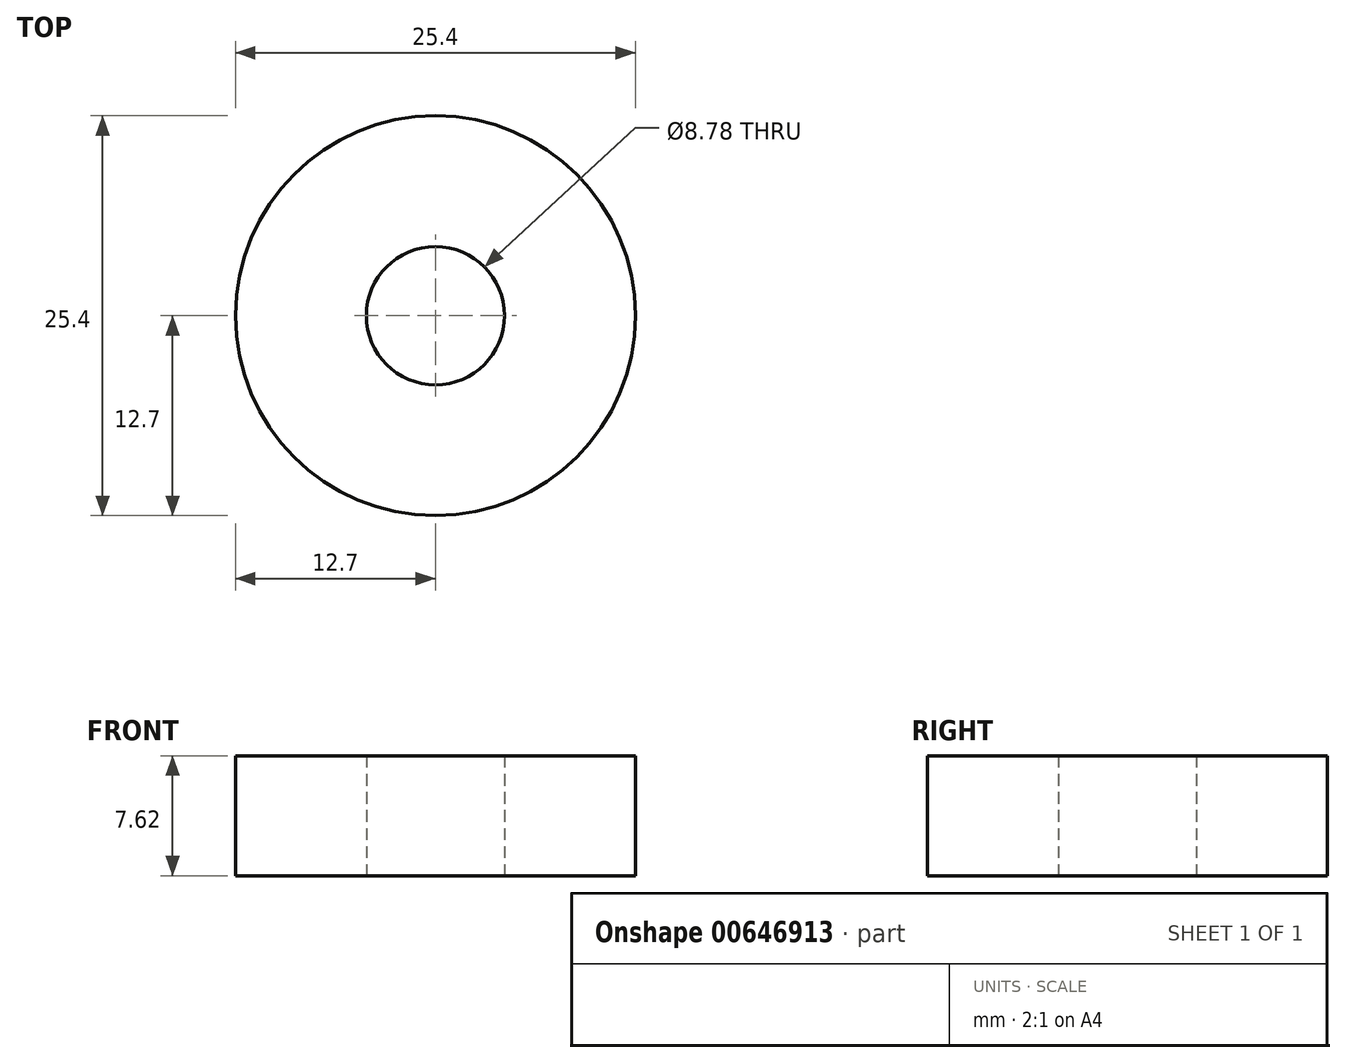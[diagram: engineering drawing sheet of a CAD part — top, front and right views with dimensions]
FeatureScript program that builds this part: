
annotation { "Feature Type Name" : "Feature", "Feature Type Description" : "" }
export const myFeature = defineFeature(function(context is Context, id is Id, definition is map)
    precondition{}
    {
        {
            var Q0;
            Q0=qCreatedBy(makeId("Top.planeOp"),FACE);
            var sketch = newSketch(context, id + "F0", { "sketchPlane" : qUnion([Q0])});
            skCircle(sketch, "E0", {"center": v(0, 0) * mm, "radius": 12.7 * mm});
            skSolve(sketch);
        }
        {
            var Q0;
            Q0 = qSketchRegion(id + "F0", true);
            extrude(context, id + "F1", {"entities" : qUnion([Q0]), "depth" : 7.62 * mm, "offsetDistance" : 25.4 * mm});
        }
        {
            var Q0;
            Q0=makeQuery(id+"F1.opExtrude","CAP_FACE",FACE,{"disambiguationData":[OSD([sQuery(id+"F0.wireOp",EDGE,"E0")])],"isStart":true});
            var sketch = newSketch(context, id + "F2", { "sketchPlane" : qUnion([Q0])});
            skCircle(sketch, "E1", {"center": v(0, 0) * mm, "radius": 4.4 * mm});
            skSolve(sketch);
        }
        {
            var Q0;
            Q0=makeQuery(id+"F2.imprint","IMPRINT",FACE,{"disambiguationData":[TD([[makeQuery(id+"F2.imprint","IMPRINT",EDGE,{"derivedFrom":sQuery(id+"F2.wireOp",EDGE,"E1")}),1.0]])]});
            extrude(context, id + "F3", {"entities" : qUnion([Q0]), "operationType" : NewBodyOperationType.REMOVE, "oppositeDirection" : true, "depth" : 25.4 * mm, "offsetDistance" : 25.4 * mm});
        }
    });
